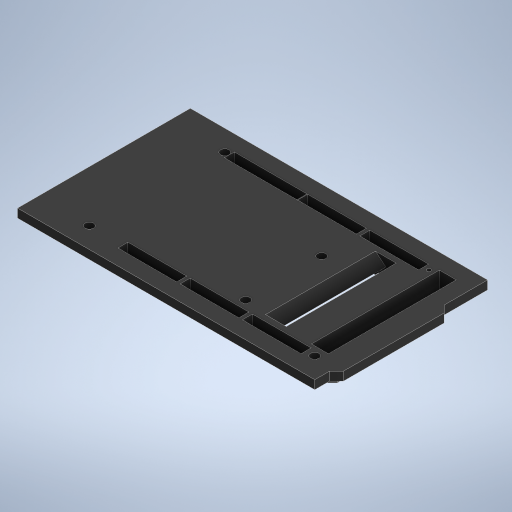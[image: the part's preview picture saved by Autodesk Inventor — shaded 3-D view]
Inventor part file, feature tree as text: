
AUTODESK INVENTOR PART (.ipt)
format: ipt  version: 2024 (Build 280153000, 153)  size: 724,480 bytes
history: native  units: in
note: dims shown in document units (in); Inventor stores cm internally (conversion verified against a paired STEP export)
features: extrude x12, sketch x12, projected_geometry x6, mirror x1
ambient origin geometry x8: Origin, YZ Plane, XZ Plane, XY Plane, X Axis, Y Axis, Z Axis, Center Point
bodies: Solid1 (feature_tree)
feature tree (31):
  extrude  "Extrusion1"  Depth=0.125in
  extrude  "Extrusion5"  Depth=0.25in TaperAngle=0.0deg
  extrude  "Extrusion6"  Depth=0.69in
  extrude  "Extrusion7"  Depth=0.0526in
  extrude  "Extrusion8"  Depth=0.06in
  mirror  "Mirror1"
  extrude  "Extrusion9"  Depth=0.1in
  extrude  "Extrusion10"  Depth=1.05in
  extrude  "Extrusion11"  Depth=0.0526in
  extrude  "Extrusion12"  Depth=0.1in
  extrude  "Extrusion13"  Depth=0.1in
  extrude  "Extrusion14"  Depth=0.2in
  extrude  "Extrusion15"  Depth=0.2in
  sketch  "Sketch12"  dims[d194=0.4959in d195=0.25in d196=0.0in]
  projected_geometry  "Projected Loop2"
  sketch  "Sketch13"  dims[d236=0.2in d237=0.69in]
  sketch  "Sketch14"  dims[d238=0.0526in d239=1.0in]
  sketch  "Sketch15"  dims[d240=0.0949in d241=0.06in]
  projected_geometry  "Projected Loop3"
  sketch  "Sketch16"  dims[d242=0.8in d243=0.1in]
  projected_geometry  "Projected Loop4"
  sketch  "Sketch17"  dims[d244=0.8in d245=1.05in]
  sketch  "Sketch18"  dims[d246=0.0526in d247=0.8in]
  sketch  "Sketch19"  dims[d248=0.0949in d249=0.1in]
  projected_geometry  "Projected Loop5"
  sketch  "Sketch20"  dims[d250=0.0526in d251=0.8in d252=0.0949in d253=0.1in d254=0.8in]
  projected_geometry  "Projected Loop6"
  sketch  "Sketch21"  dims[d255=0.0026in d256=0.1026in d257=0.1949in d258=1.8in d259=0.25in d260=0.0in d261=0.25in d262=0.0in d263=1.0in d264=0.0in d265=0.025in d266=0.025in d267=0.025in d268=0.025in d269=0.025in d270=0.025in d271=0.025in d272=0.025in d273=1.0in d274=0.0in d275=0.0591in d276=0.0in d277=0.0in d278=0.4in d279=0.3in d280=0.2749in d281=1.0in d282=0.0in d283=0.25in d284=0.0in d285=0.0in d286=0.0in d287=0.125in d288=0.125in d289=0.125in d290=0.125in d291=0.125in d292=0.0in d293=0.2in d294=0.0in]
  projected_geometry  "Projected Loop7"
  sketch  "Sketch3"  dims[d74=2.1in d75=0.125in d76=0.075in d77=0.3543in d78=0.3661in d79=0.25in d80=0.474in d81=3.9in d82=3.9in d83=0.5382in d84=0.1in d85=0.6in d86=0.1in d87=0.35in d88=0.1in d89=0.1in d90=0.1in d91=0.7in d92=1.3in d93=1.3in d94=0.3in d95=0.51in d96=0.1in d97=0.1in d98=0.1in d99=0.1in d100=0.1in d101=0.125in d102=0.125in d103=0.125in d104=0.125in d105=0.125in d106=0.125in d107=0.2in d108=0.125in d109=0.2in d110=0.125in]
  sketch  "Sketch5"  dims[d148=2.1in d149=0.125in d150=0.075in d151=0.3543in d152=0.3661in d153=0.25in d154=0.474in d155=3.9in d156=3.9in d157=0.5382in d158=0.1in d159=0.6in d160=0.1in d161=0.35in d162=0.1in d163=0.1in d164=0.1in d165=0.7in d166=1.3in d167=1.3in d168=0.3in d169=0.51in d170=0.1in d171=0.1in d172=0.1in d173=0.1in d174=0.1in d175=0.125in d176=0.125in d177=0.125in d178=0.125in d179=0.125in d180=0.125in d181=0.2in d182=0.125in d183=0.2in d184=0.125in d185=0.125in d186=0.0in d193=0.3996in]
